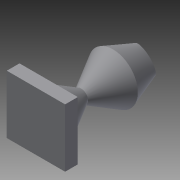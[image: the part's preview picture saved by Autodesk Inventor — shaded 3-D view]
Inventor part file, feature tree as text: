
AUTODESK INVENTOR PART (.ipt)
format: ipt  version: 2015 (Build 190159000, 159)  size: 230,400 bytes
history: native  units: mm
features: sketch x5, plane x4, loft x3, other x2, shell x1, extrude x1
ambient origin geometry x8: Origin, YZ Plane, XZ Plane, XY Plane, X Axis, Y Axis, Z Axis, Center Point
bodies: Solid1 (feature_tree)
feature tree (16):
  sketch  "Sketch1"  dims[d0=5.0mm d1=0.0mm d2=90.0deg]
  plane  "Work Plane1"
  plane  "Work Plane2"
  loft  "Loft1"
  plane  "Work Plane3"
  loft  "Loft2"
  plane  "Work Plane4"
  loft  "Loft3"
  shell  "Shell3"  Thickness=5.0mm
  extrude  "Extrusion1"  TaperAngle=0.0deg  [1 undecoded]
  sketch  "Sketch2"  dims[d3=0.0mm d4=90.0deg d5=5.0mm]
  sketch  "Sketch3"  dims[d6=0.0mm d7=90.0deg d8=0.0mm d9=90.0deg d10=5.0mm]
  other  "Edges1"
  sketch  "Sketch4"  dims[d11=0.0mm d12=90.0deg d13=0.0mm d14=90.0deg]
  other  "Edges2"
  sketch  "Sketch5"  dims[d17=0.5mm d18=2.0mm d19=0.0mm]
note: 1 required parameter value undecoded (feature->parameter linkage not recoverable at this tier; creation-order binding heuristic only, values carry confidence <= 0.55)
